# Revit family: Haworth_Cappellini_HiPad_Stool_AP_PRELIMINARY
name_source: partatom
category: Furniture
revit_build: Autodesk Revit 2018 (Build: 20170223_1515(x64)
units: mm (PartAtom-declared; Revit-internal decimal feet)

## family parameters
Always vertical = Yes
Cut with Voids When Loaded = No
OmniClass Number = 23.40.70.14.64.21
OmniClass Title = Systems Furniture
Room Calculation Point = No
Shared = No
Work Plane-Based = No

## types (3) — shared parameters
Actual Depth = 350 mm  [stored 1.14829 ft]
Actual Width = 440 mm  [stored 1.44357 ft]
Assembly Code = E2020200
Description = Haworth - Cappellini - Hi-Pad - Stool
Glide Finish = Haworth _ Polymer _ Black
Manufacturer = Haworth
Model = HP_1X
Revision Number = 8
Size = Verify Final Dim. w/ Haworth
URL = https://www.haworth.com
URL - Product = https://www.haworth.com
Warranty = http://www.haworth.com

## per-type parameters (varying)
| type | Actual Height | Bar Height | High | Low | Medium | Seat Height Offset |
| High Stool | 800 mm  [stored 2.62467 ft] | 381 mm  [stored 1.25 ft] | Yes | No | No | 705 mm  [stored 2.31299 ft] |
| Medium Stool | 700 mm  [stored 2.29659 ft] | 280 mm  [stored 0.918635 ft] | No | No | Yes | 610 mm  [stored 2.00131 ft] |
| Low Stool | 450 mm  [stored 1.47638 ft] | 280 mm  [stored 0.918635 ft] | No | Yes | No | 377 mm |

note: [stored X ft] marks values corroborated as IEEE doubles in the binary element streams (Revit-internal decimal feet)

## geometry (parser evidence)
native form markers: Sweep x12
no freeform markers — native parametric forms only
